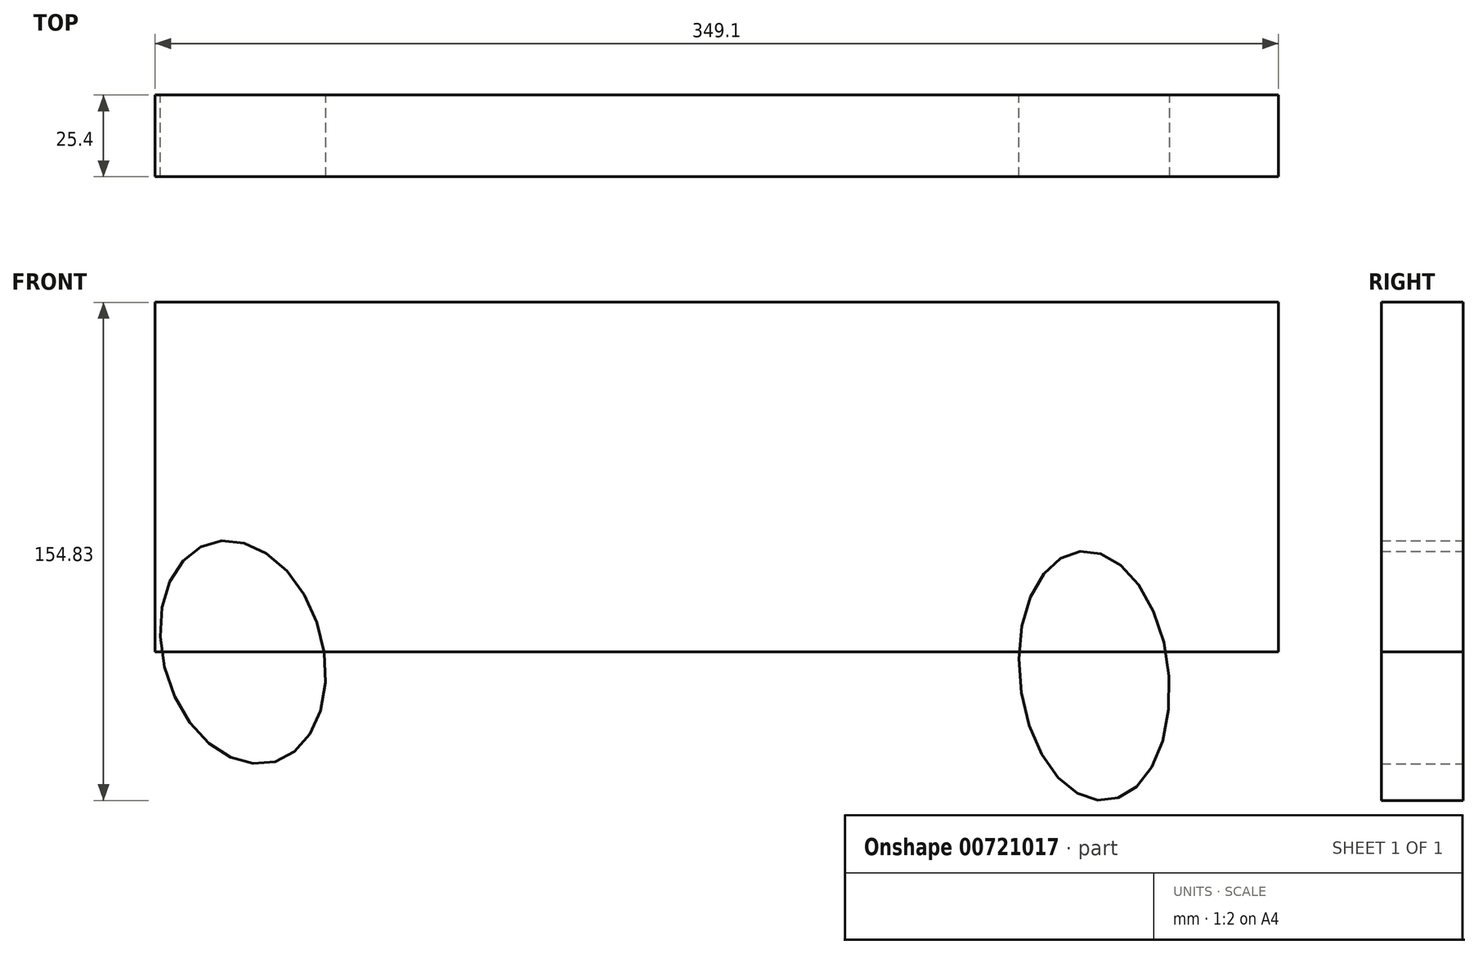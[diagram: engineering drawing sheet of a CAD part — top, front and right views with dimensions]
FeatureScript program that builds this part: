
annotation { "Feature Type Name" : "Feature", "Feature Type Description" : "" }
export const myFeature = defineFeature(function(context is Context, id is Id, definition is map)
    precondition{}
    {
        {
            var Q0;
            Q0=qCreatedBy(makeId("Front.planeOp"),FACE);
            var sketch = newSketch(context, id + "F0", { "sketchPlane" : qUnion([Q0])});
            skLineSegment(sketch, "E0.bottom", {"start": v(-174.55, 54.34) * mm, "end": v(174.55, 54.34) * mm});
            skLineSegment(sketch, "E0.top", {"start": v(-174.55, -54.34) * mm, "end": v(174.55, -54.34) * mm});
            skLineSegment(sketch, "E0.left", {"start": v(-174.55, 54.34) * mm, "end": v(-174.55, -54.34) * mm});
            skLineSegment(sketch, "E0.right", {"start": v(174.55, 54.34) * mm, "end": v(174.55, -54.34) * mm});
            skPoint(sketch, "E0.middle", {"position": v(0, 0) * mm});
            skSolve(sketch);
        }
        {
            var Q0;
            Q0=qCreatedBy(makeId("Front.planeOp"),FACE);
            var sketch = newSketch(context, id + "F1", { "sketchPlane" : qUnion([Q0])});
            skLineSegment(sketch, "E1", {"start": v(174.55, 54.5) * mm, "end": v(298.15, 62.43) * mm});
            skLineSegment(sketch, "E2", {"start": v(298.15, 62.43) * mm, "end": v(293.38, 18.56) * mm});
            skLineSegment(sketch, "E3", {"start": v(293.38, 18.56) * mm, "end": v(249.14, 11.86) * mm});
            skLineSegment(sketch, "E4", {"start": v(249.14, 11.86) * mm, "end": v(244.8, -22.35) * mm});
            skLineSegment(sketch, "E5", {"start": v(244.8, -22.35) * mm, "end": v(293.38, -15.46) * mm});
            skLineSegment(sketch, "E6", {"start": v(291.21, -15.46) * mm, "end": v(281.24, -52.17) * mm});
            skLineSegment(sketch, "E7", {"start": v(281.24, -52.17) * mm, "end": v(179.32, -52.17) * mm});
            skEllipse(sketch, "E8", {"center": v(-147.23, -54.43) * mm, "majorRadius": 35.42 * mm, "minorRadius": 24.73 * mm, "majorAxis": v(0.28, -0.96)});
            skEllipse(sketch, "E9", {"center": v(117.3, -61.76) * mm, "majorRadius": 38.89 * mm, "minorRadius": 23.17 * mm, "majorAxis": v(-0.11, 1)});
            skSolve(sketch);
        }
        {
            var Q0;
            Q0=makeQuery(id+"F0.imprint","IMPRINT",FACE,{"disambiguationData":[TD([[makeQuery(id+"F0.imprint","IMPRINT",EDGE,{"derivedFrom":sQuery(id+"F0.wireOp",EDGE,"E0.bottom")}),-1.0]])]});
            var Q1;
            Q1=makeQuery(id+"F1.imprint","IMPRINT",FACE,{"disambiguationData":[TD([[makeQuery(id+"F1.imprint","IMPRINT",EDGE,{"derivedFrom":sQuery(id+"F1.wireOp",EDGE,"E9")}),1.0]])]});
            var Q2;
            Q2=makeQuery(id+"F1.imprint","IMPRINT",FACE,{"disambiguationData":[TD([[makeQuery(id+"F1.imprint","IMPRINT",EDGE,{"derivedFrom":sQuery(id+"F1.wireOp",EDGE,"E8")}),1.0]])]});
            extrude(context, id + "F2", {"entities" : qUnion([Q0, Q1, Q2]), "depth" : 25.4 * mm, "offsetDistance" : 25.4 * mm});
        }
    });
